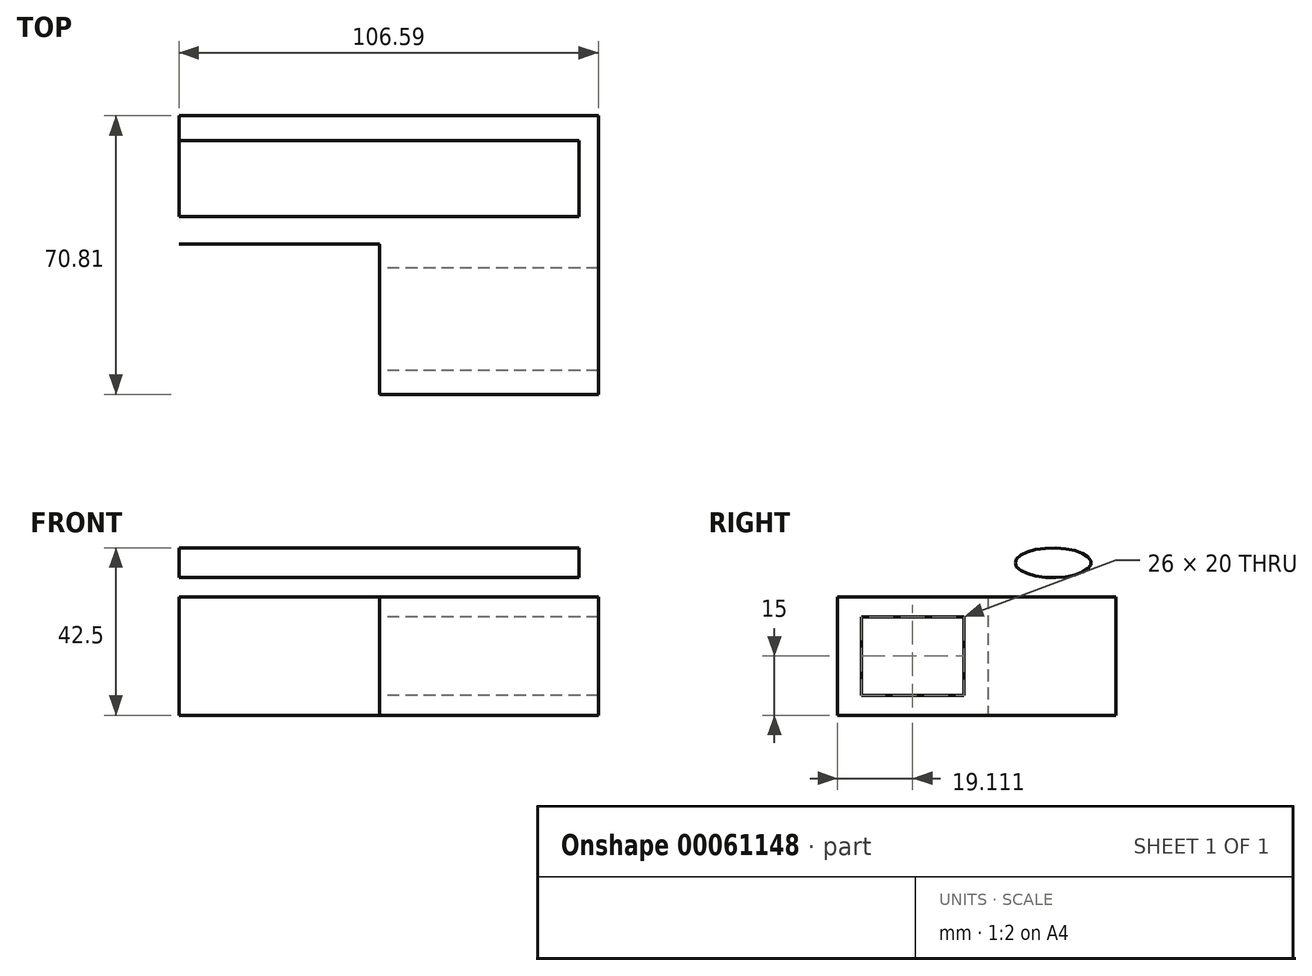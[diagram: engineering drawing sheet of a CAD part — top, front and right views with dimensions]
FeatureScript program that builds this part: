
annotation { "Feature Type Name" : "Feature", "Feature Type Description" : "" }
export const myFeature = defineFeature(function(context is Context, id is Id, definition is map)
    precondition{}
    {
        {
            var Q0;
            Q0=qCreatedBy(makeId("Top.planeOp"),FACE);
            var sketch = newSketch(context, id + "F0", { "sketchPlane" : qUnion([Q0])});
            skLineSegment(sketch, "E0", {"start": v(-58.89, 32.59) * mm, "end": v(47.7, 32.59) * mm});
            skLineSegment(sketch, "E1", {"start": v(-7.88, -38.22) * mm, "end": v(-7.88, 0) * mm});
            skLineSegment(sketch, "E2", {"start": v(-7.88, 0) * mm, "end": v(-58.89, 0) * mm});
            skLineSegment(sketch, "E3", {"start": v(-58.89, 0) * mm, "end": v(-58.89, 32.59) * mm});
            skLineSegment(sketch, "E4", {"start": v(47.7, 32.59) * mm, "end": v(47.7, -38.22) * mm});
            skLineSegment(sketch, "E5", {"start": v(47.7, -38.22) * mm, "end": v(-7.88, -38.22) * mm});
            skSolve(sketch);
        }
        {
            var Q0;
            Q0 = qSketchRegion(id + "F0", true);
            extrude(context, id + "F1", {"entities" : qUnion([Q0]), "depth" : 30 * mm});
        }
        {
            var Q0;
            Q0=makeQuery(id+"F1.opExtrude","SWEPT_FACE",FACE,{"disambiguationData":[OSD([sQuery(id+"F0.wireOp",EDGE,"E1")])]});
            var sketch = newSketch(context, id + "F2", { "sketchPlane" : qUnion([Q0])});
            skLineSegment(sketch, "E6.rect.bottom", {"start": v(32.1, 5) * mm, "end": v(6.1, 5) * mm});
            skLineSegment(sketch, "E6.rect.top", {"start": v(32.1, 25) * mm, "end": v(6.1, 25) * mm});
            skLineSegment(sketch, "E6.rect.left", {"start": v(32.1, 5) * mm, "end": v(32.1, 25) * mm});
            skLineSegment(sketch, "E6.rect.right", {"start": v(6.1, 5) * mm, "end": v(6.1, 25) * mm});
            skPoint(sketch, "E6.rect.middle", {"position": v(19.1, 15) * mm});
            skPoint(sketch, "E6.rect.middle.positionSnap0", {"position": v(38.22, 15) * mm});
            skPoint(sketch, "E6.rect.middle.positionSnap1", {"position": v(19.1, 30) * mm});
            skPoint(sketch, "E6.rect.centerSnap0", {"position": v(38.22, 15) * mm});
            skPoint(sketch, "E6.rect.centerSnap1", {"position": v(19.1, 30) * mm});
            skSolve(sketch);
        }
        {
            var Q0;
            Q0=makeQuery(id+"F2.imprint","IMPRINT",FACE,{"disambiguationData":[TD([[makeQuery(id+"F2.imprint","IMPRINT",EDGE,{"derivedFrom":sQuery(id+"F2.wireOp",EDGE,"E6.rect.bottom")}),-1.0]])]});
            extrude(context, id + "F3", {"entities" : qUnion([Q0]), "operationType" : NewBodyOperationType.REMOVE, "endBound" : BoundingType.THROUGH_ALL, "oppositeDirection" : true, "depth" : 25 * mm});
        }
        {
            var Q0;
            Q0=makeQuery(id+"F1.opExtrude","SWEPT_FACE",FACE,{"disambiguationData":[OSD([sQuery(id+"F0.wireOp",EDGE,"E3")])]});
            var sketch = newSketch(context, id + "F4", { "sketchPlane" : qUnion([Q0])});
            skEllipse(sketch, "E7", {"center": v(-16.58, 38.73) * mm, "majorRadius": 9.64 * mm, "minorRadius": 3.77 * mm, "majorAxis": v(1, 0)});
            skSolve(sketch);
        }
        {
            var Q0;
            Q0 = qSketchRegion(id + "F4", true);
            extrude(context, id + "F5", {"entities" : qUnion([Q0]), "oppositeDirection" : true, "depth" : 101.63 * mm});
        }
    });
